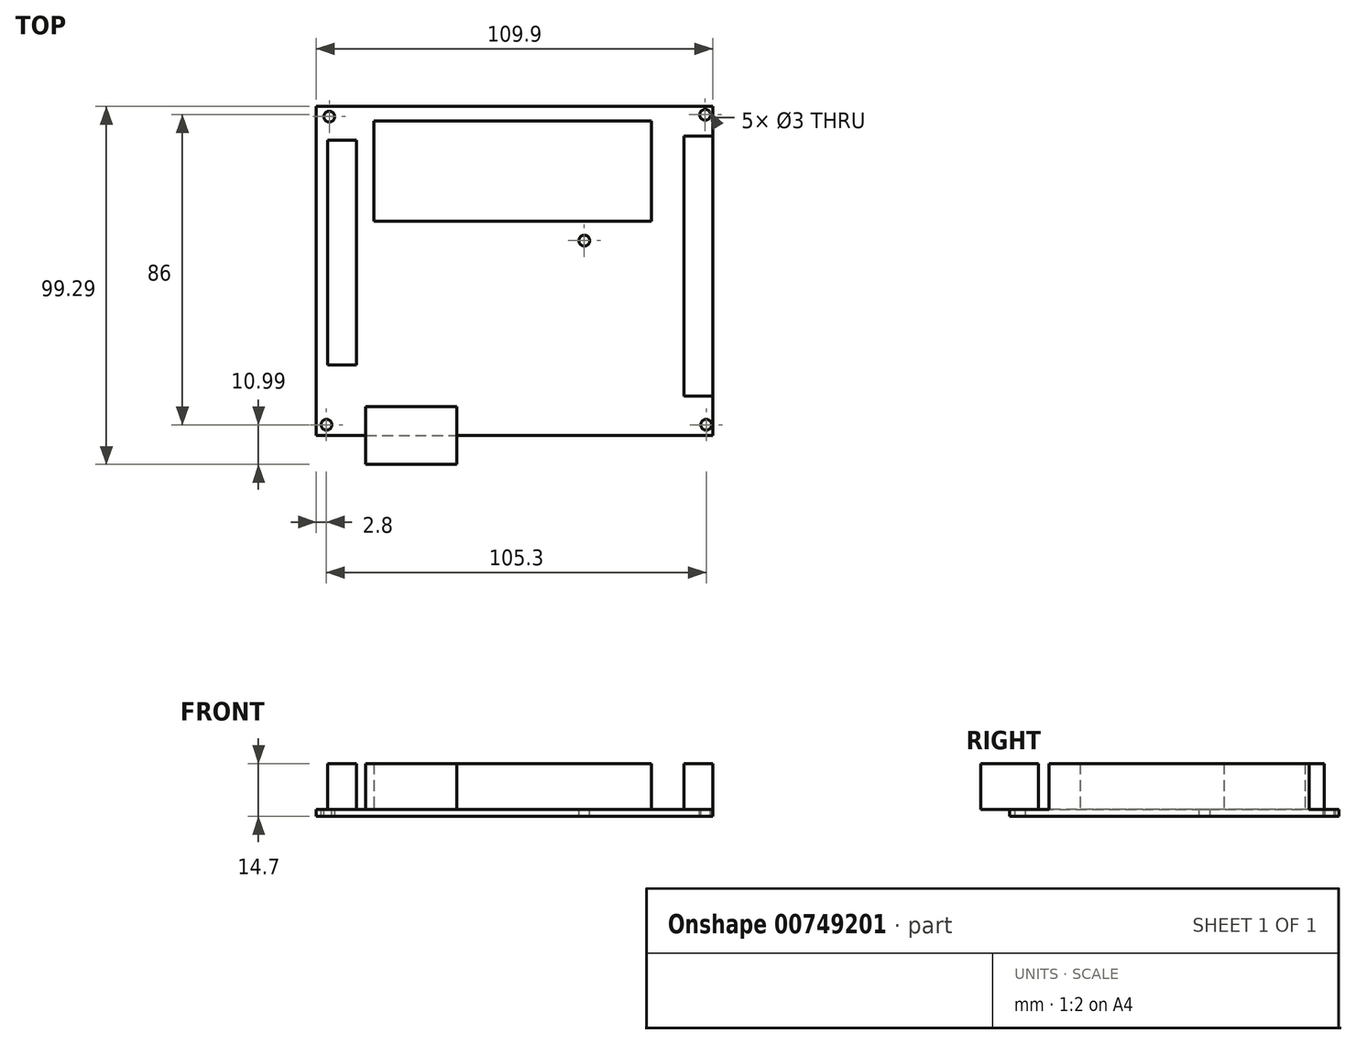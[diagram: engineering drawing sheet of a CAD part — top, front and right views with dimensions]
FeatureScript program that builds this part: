
annotation { "Feature Type Name" : "Feature", "Feature Type Description" : "" }
export const myFeature = defineFeature(function(context is Context, id is Id, definition is map)
    precondition{}
    {
        {
            var Q0;
            Q0=qCreatedBy(makeId("Top.planeOp"),FACE);
            var sketch = newSketch(context, id + "F0", { "sketchPlane" : qUnion([Q0])});
            skLineSegment(sketch, "E0.bottom", {"start": v(0, 0) * mm, "end": v(109.9, 0) * mm});
            skLineSegment(sketch, "E0.top", {"start": v(0, 91.3) * mm, "end": v(109.9, 91.3) * mm});
            skLineSegment(sketch, "E0.left", {"start": v(0, 0) * mm, "end": v(0, 91.3) * mm});
            skLineSegment(sketch, "E0.right", {"start": v(109.9, 0) * mm, "end": v(109.9, 91.3) * mm});
            skSolve(sketch);
        }
        {
            var Q0;
            Q0=qSketchRegion(id+"F0",true);
            extrude(context, id + "F1", {"entities" : qUnion([Q0]), "depth" : 2 * mm, "offsetDistance" : 25.4 * mm});
        }
        {
            var Q0;
            Q0=makeQuery(id+"F1.opExtrude","CAP_FACE",FACE,{"disambiguationData":[OSD([sQuery(id+"F0.wireOp",EDGE,"E0.bottom"),sQuery(id+"F0.wireOp",EDGE,"E0.top"),sQuery(id+"F0.wireOp",EDGE,"E0.left"),sQuery(id+"F0.wireOp",EDGE,"E0.right")])],"isStart":false});
            var sketch = newSketch(context, id + "F2", { "sketchPlane" : qUnion([Q0])});
            skCircle(sketch, "E1", {"center": v(3.6, 88.5) * mm, "radius": 1.5 * mm});
            skCircle(sketch, "E2", {"center": v(108.1, 3) * mm, "radius": 1.5 * mm});
            skCircle(sketch, "E3", {"center": v(107.8, 89) * mm, "radius": 1.5 * mm});
            skCircle(sketch, "E4", {"center": v(2.8, 3) * mm, "radius": 1.5 * mm});
            skCircle(sketch, "E5", {"center": v(74.3, 54.1) * mm, "radius": 1.5 * mm});
            skSolve(sketch);
        }
        {
            var Q0;
            Q0=qSketchRegion(id+"F2",true);
            extrude(context, id + "F3", {"entities" : qUnion([Q0]), "operationType" : NewBodyOperationType.REMOVE, "oppositeDirection" : true, "depth" : 25.4 * mm, "offsetDistance" : 25.4 * mm});
        }
        {
            var Q0;
            Q0=makeQuery(id+"F1.opExtrude","CAP_FACE",FACE,{"disambiguationData":[OSD([sQuery(id+"F0.wireOp",EDGE,"E0.bottom"),sQuery(id+"F0.wireOp",EDGE,"E0.top"),sQuery(id+"F0.wireOp",EDGE,"E0.left"),sQuery(id+"F0.wireOp",EDGE,"E0.right")])],"isStart":false});
            var sketch = newSketch(context, id + "F4", { "sketchPlane" : qUnion([Q0])});
            skLineSegment(sketch, "E6.bottom", {"start": v(13.68, 8.06) * mm, "end": v(38.98, 8.06) * mm});
            skLineSegment(sketch, "E6.top", {"start": v(13.68, -7.99) * mm, "end": v(38.98, -7.99) * mm});
            skLineSegment(sketch, "E6.left", {"start": v(13.68, 8.06) * mm, "end": v(13.68, -7.99) * mm});
            skLineSegment(sketch, "E6.right", {"start": v(38.98, 8.06) * mm, "end": v(38.98, -7.99) * mm});
            skSolve(sketch);
        }
        {
            var Q0;
            Q0=qSketchRegion(id+"F4",true);
            extrude(context, id + "F5", {"entities" : qUnion([Q0]), "operationType" : NewBodyOperationType.ADD, "depth" : 12.7 * mm, "offsetDistance" : 25.4 * mm});
        }
        {
            var Q0;
            Q0=makeQuery(id+"F1.opExtrude","CAP_FACE",FACE,{"disambiguationData":[OSD([sQuery(id+"F0.wireOp",EDGE,"E0.bottom"),sQuery(id+"F0.wireOp",EDGE,"E0.top"),sQuery(id+"F0.wireOp",EDGE,"E0.left"),sQuery(id+"F0.wireOp",EDGE,"E0.right")])],"isStart":false});
            var sketch = newSketch(context, id + "F6", { "sketchPlane" : qUnion([Q0])});
            skLineSegment(sketch, "E7.bottom", {"start": v(3.2, 81.95) * mm, "end": v(11.14, 81.95) * mm});
            skLineSegment(sketch, "E7.top", {"start": v(3.2, 19.55) * mm, "end": v(11.14, 19.55) * mm});
            skLineSegment(sketch, "E7.left", {"start": v(3.2, 81.95) * mm, "end": v(3.2, 19.55) * mm});
            skLineSegment(sketch, "E7.right", {"start": v(11.14, 81.95) * mm, "end": v(11.14, 19.55) * mm});
            skSolve(sketch);
        }
        {
            var Q0;
            Q0=qSketchRegion(id+"F6",true);
            extrude(context, id + "F7", {"entities" : qUnion([Q0]), "operationType" : NewBodyOperationType.ADD, "depth" : 12.7 * mm, "offsetDistance" : 25.4 * mm});
        }
        {
            var Q0;
            Q0=makeQuery(id+"F1.opExtrude","CAP_FACE",FACE,{"disambiguationData":[OSD([sQuery(id+"F0.wireOp",EDGE,"E0.bottom"),sQuery(id+"F0.wireOp",EDGE,"E0.top"),sQuery(id+"F0.wireOp",EDGE,"E0.left"),sQuery(id+"F0.wireOp",EDGE,"E0.right")])],"isStart":false});
            var sketch = newSketch(context, id + "F8", { "sketchPlane" : qUnion([Q0])});
            skLineSegment(sketch, "E8.bottom", {"start": v(101.93, 83.13) * mm, "end": v(109.9, 83.13) * mm});
            skLineSegment(sketch, "E8.top", {"start": v(101.93, 10.94) * mm, "end": v(109.9, 10.94) * mm});
            skLineSegment(sketch, "E8.left", {"start": v(101.93, 83.13) * mm, "end": v(101.93, 10.94) * mm});
            skLineSegment(sketch, "E8.right", {"start": v(109.9, 83.13) * mm, "end": v(109.9, 10.94) * mm});
            skLineSegment(sketch, "E9.bottom", {"start": v(92.86, 87.32) * mm, "end": v(15.92, 87.32) * mm});
            skLineSegment(sketch, "E9.top", {"start": v(92.86, 59.42) * mm, "end": v(15.92, 59.42) * mm});
            skLineSegment(sketch, "E9.left", {"start": v(92.86, 87.32) * mm, "end": v(92.86, 59.42) * mm});
            skLineSegment(sketch, "E9.right", {"start": v(15.92, 87.32) * mm, "end": v(15.92, 59.42) * mm});
            skSolve(sketch);
        }
        {
            var Q0;
            Q0=qSketchRegion(id+"F8",true);
            extrude(context, id + "F9", {"entities" : qUnion([Q0]), "operationType" : NewBodyOperationType.ADD, "depth" : 12.7 * mm, "offsetDistance" : 25.4 * mm});
        }
    });
